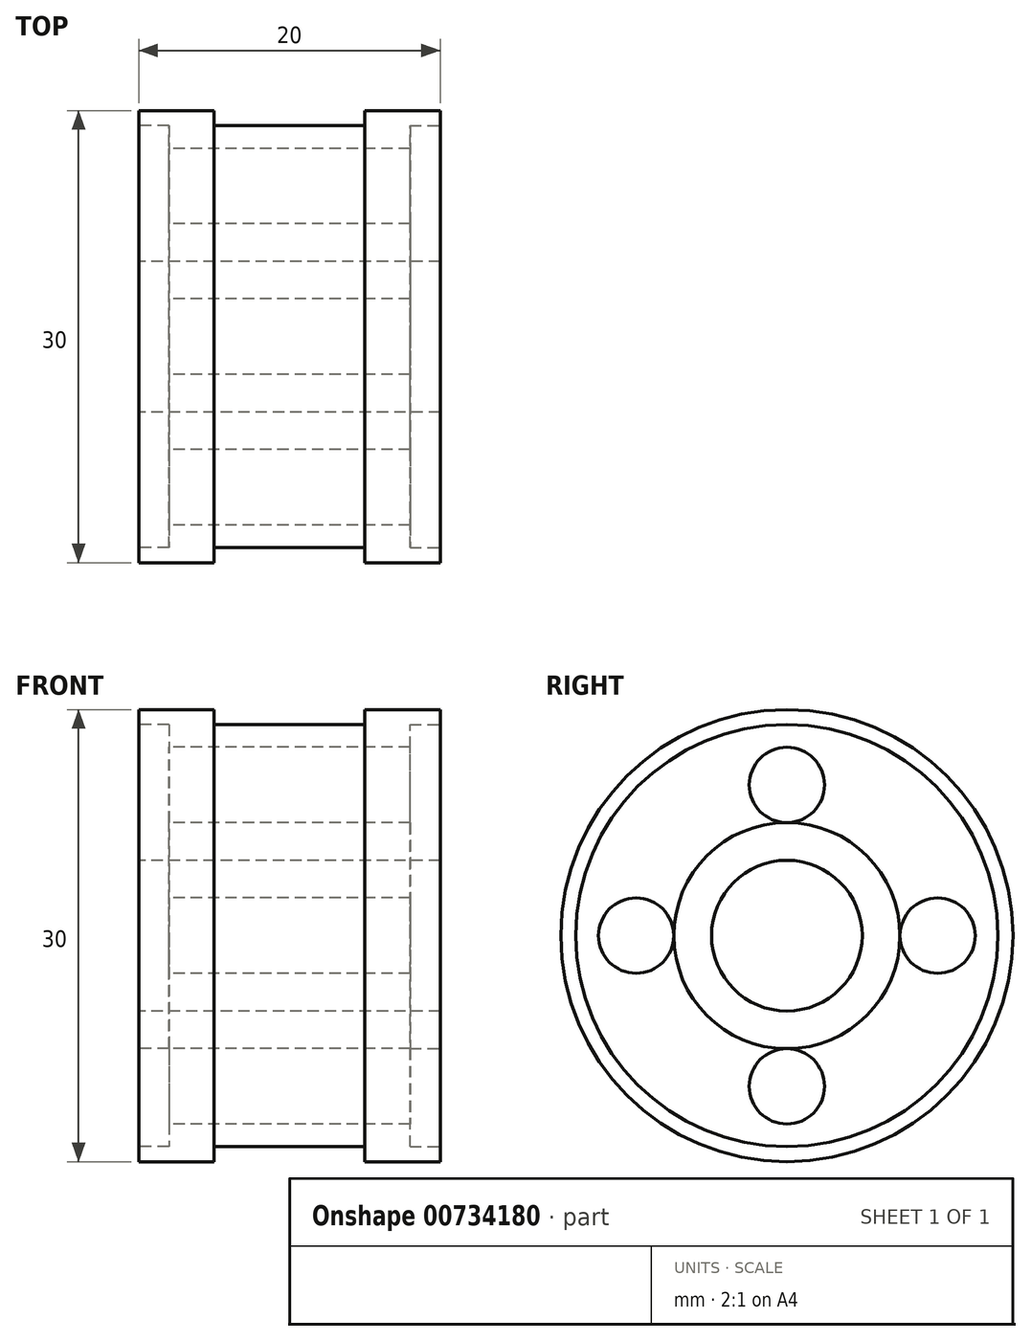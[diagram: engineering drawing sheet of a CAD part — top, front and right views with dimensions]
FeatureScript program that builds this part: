
annotation { "Feature Type Name" : "Feature", "Feature Type Description" : "" }
export const myFeature = defineFeature(function(context is Context, id is Id, definition is map)
    precondition{}
    {
        {
            var Q0;
            Q0=qCreatedBy(makeId("Top.planeOp"),FACE);
            var sketch = newSketch(context, id + "F0", { "sketchPlane" : qUnion([Q0])});
            skLineSegment(sketch, "E0", {"start": v(12.04, 15) * mm, "end": v(7.04, 15) * mm});
            skLineSegment(sketch, "E1", {"start": v(-2.96, 15) * mm, "end": v(-7.96, 15) * mm});
            skLineSegment(sketch, "E2", {"start": v(-22.87, 0) * mm, "end": v(18.63, 0) * mm});
            skLineSegment(sketch, "E3", {"start": v(7.04, 15) * mm, "end": v(7.04, 14) * mm});
            skLineSegment(sketch, "E4", {"start": v(7.04, 14) * mm, "end": v(-2.96, 14) * mm});
            skLineSegment(sketch, "E5", {"start": v(-2.96, 15) * mm, "end": v(-2.96, 14) * mm});
            skLineSegment(sketch, "E6", {"start": v(-7.96, 5) * mm, "end": v(12.04, 5) * mm});
            skLineSegment(sketch, "E7", {"start": v(-7.96, 15) * mm, "end": v(-7.96, 5) * mm});
            skLineSegment(sketch, "E8", {"start": v(12.04, 15) * mm, "end": v(12.04, 5) * mm});
            skSolve(sketch);
        }
        {
            var Q0;
            Q0=makeQuery(id+"F0.imprint","IMPRINT",FACE,{"disambiguationData":[TD([[makeQuery(id+"F0.imprint","IMPRINT",EDGE,{"derivedFrom":sQuery(id+"F0.wireOp",EDGE,"E0")}),1.0]])]});
            var Q1;
            Q1=sQuery(id+"F0.wireOp",EDGE,"E2");
            revolve(context, id + "F1", {"surfaceOperationType" : NewSurfaceOperationType.NEW, "entities" : qUnion([Q0]), "axis" : qUnion([Q1]), "revolveType" : RevolveType.FULL});
        }
        {
            var Q0;
            Q0=makeQuery(id+"F1.opRevolve","SWEPT_FACE",FACE,{"disambiguationData":[OSD([sQuery(id+"F0.wireOp",EDGE,"E7")])]});
            var sketch = newSketch(context, id + "F2", { "sketchPlane" : qUnion([Q0])});
            skCircle(sketch, "E9", {"center": v(0, 10) * mm, "radius": 2.5 * mm});
            skCircle(sketch, "E10.1.0", {"center": v(-10, 0) * mm, "radius": 2.5 * mm});
            skCircle(sketch, "E10.2.0", {"center": v(0, -10) * mm, "radius": 2.5 * mm});
            skCircle(sketch, "E10.3.0", {"center": v(10, 0) * mm, "radius": 2.5 * mm});
            skPoint(sketch, "E10.center", {"position": v(0, 0) * mm});
            skSolve(sketch);
        }
        {
            var Q0;
            Q0=makeQuery(id+"F2.imprint","IMPRINT",FACE,{"disambiguationData":[TD([[makeQuery(id+"F2.imprint","IMPRINT",EDGE,{"derivedFrom":sQuery(id+"F2.wireOp",EDGE,"E10.1.0")}),1.0]])]});
            var Q1;
            Q1=makeQuery(id+"F2.imprint","IMPRINT",FACE,{"disambiguationData":[TD([[makeQuery(id+"F2.imprint","IMPRINT",EDGE,{"derivedFrom":sQuery(id+"F2.wireOp",EDGE,"E10.3.0")}),1.0]])]});
            var Q2;
            Q2=makeQuery(id+"F2.imprint","IMPRINT",FACE,{"disambiguationData":[TD([[makeQuery(id+"F2.imprint","IMPRINT",EDGE,{"derivedFrom":sQuery(id+"F2.wireOp",EDGE,"E9")}),1.0]])]});
            var Q3;
            Q3=makeQuery(id+"F2.imprint","IMPRINT",FACE,{"disambiguationData":[TD([[makeQuery(id+"F2.imprint","IMPRINT",EDGE,{"derivedFrom":sQuery(id+"F2.wireOp",EDGE,"E10.2.0")}),1.0]])]});
            extrude(context, id + "F3", {"entities" : qUnion([Q0, Q1, Q2, Q3]), "operationType" : NewBodyOperationType.REMOVE, "endBound" : BoundingType.THROUGH_ALL, "oppositeDirection" : true, "depth" : 25 * mm, "offsetDistance" : 25 * mm});
        }
        {
            var Q0;
            Q0=makeQuery(id+"F1.opRevolve","SWEPT_FACE",FACE,{"disambiguationData":[OSD([sQuery(id+"F0.wireOp",EDGE,"E7")])]});
            cPlane(context, id + "F4", {"entities" : qUnion([Q0]), "cplaneType" : CPlaneType.OFFSET, "offset" : 1 * mm, "width" : 150 * mm, "height" : 150 * mm});
        }
        {
            var Q0;
            Q0=qCreatedBy(id+"F4.planeOp",FACE);
            var sketch = newSketch(context, id + "F5", { "sketchPlane" : qUnion([Q0])});
            skCircle(sketch, "E11", {"center": v(0, 0) * mm, "radius": 14 * mm});
            skCircle(sketch, "E12", {"center": v(0, 0) * mm, "radius": 7.5 * mm});
            skSolve(sketch);
        }
        {
            var Q0;
            Q0=makeQuery(id+"F5.imprint","IMPRINT",FACE,{"disambiguationData":[TD([[makeQuery(id+"F5.imprint","IMPRINT",EDGE,{"derivedFrom":sQuery(id+"F5.wireOp",EDGE,"E11")}),1.0]])]});
            extrude(context, id + "F6", {"entities" : qUnion([Q0]), "operationType" : NewBodyOperationType.REMOVE, "oppositeDirection" : true, "depth" : 3 * mm, "offsetDistance" : 25 * mm});
        }
        {
            var Q0;
            Q0=makeQuery(id+"F1.opRevolve","SWEPT_FACE",FACE,{"disambiguationData":[OSD([sQuery(id+"F0.wireOp",EDGE,"E8")])]});
            cPlane(context, id + "F7", {"entities" : qUnion([Q0]), "cplaneType" : CPlaneType.OFFSET, "offset" : 1 * mm, "width" : 150 * mm, "height" : 150 * mm});
        }
        {
            var Q0;
            Q0=qCreatedBy(id+"F7.planeOp",FACE);
            var sketch = newSketch(context, id + "F8", { "sketchPlane" : qUnion([Q0])});
            skCircle(sketch, "E13", {"center": v(0, 0) * mm, "radius": 14 * mm});
            skCircle(sketch, "E14", {"center": v(0, 0) * mm, "radius": 7.5 * mm});
            skSolve(sketch);
        }
        {
            var Q0;
            Q0 = qSketchRegion(id + "F8", true);
            extrude(context, id + "F9", {"entities" : qUnion([Q0]), "operationType" : NewBodyOperationType.REMOVE, "oppositeDirection" : true, "depth" : 3 * mm, "offsetDistance" : 25 * mm});
        }
    });
